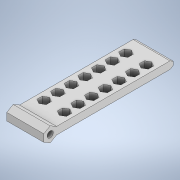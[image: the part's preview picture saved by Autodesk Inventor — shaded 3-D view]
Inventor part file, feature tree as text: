
AUTODESK INVENTOR PART (.ipt)
format: ipt  version: 2020 (Build 240168000, 168)  size: 293,888 bytes
history: native  units: in
note: dims shown in document units (in); Inventor stores cm internally (conversion verified against a paired STEP export)
features: sketch x4, extrude x3, plane x1, projected_geometry x1
ambient origin geometry x8: Origin, YZ Plane, XZ Plane, XY Plane, X Axis, Y Axis, Z Axis, Center Point
bodies: Solid1 (feature_tree)
feature tree (9):
  extrude  "Extrusion1"  Depth=2.7559in
  plane  "Work Plane1"
  extrude  "Extrusion2"  Depth=0.7874in
  extrude  "Extrusion3"  Depth=0.0787in
  sketch  "Sketch4"  dims[d6=0.7874in d7=0.0in d8=0.0787in d9=0.0787in d10=0.0787in d11=0.2273in d12=3.937in d14=0.2903in d15=0.3937in d17=0.3937in d19=3.937in d21=0.2903in d22=0.3937in d24=0.3937in d26=0.7874in d27=0.0in d28=2.4831in]
  sketch  "Sketch1"  dims[d0=0.1575in d1=2.7559in]
  sketch  "Sketch2"  dims[d2=0.1299in d3=0.7874in]
  sketch  "Sketch3"  dims[d4=0.0in d5=0.0787in]
  projected_geometry  "Projected Loop1"
